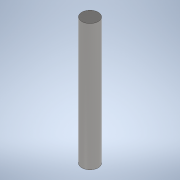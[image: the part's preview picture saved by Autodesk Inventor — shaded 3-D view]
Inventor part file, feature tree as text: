
AUTODESK INVENTOR PART (.ipt)
format: ipt  version: 2022 (Build 260153000, 153)  size: 92,672 bytes
history: native  units: mm
features: extrude x1, sketch x1
ambient origin geometry x8: Origin, YZ Plane, XZ Plane, XY Plane, X Axis, Y Axis, Z Axis, Center Point
bodies: Solid1 (feature_tree)
feature tree (2):
  extrude  "Extrusion1"  Depth=62.0mm TaperAngle=0.0deg
  sketch  "Sketch1"  dims[d0=8.0mm d1=62.0mm d2=0.0mm]
